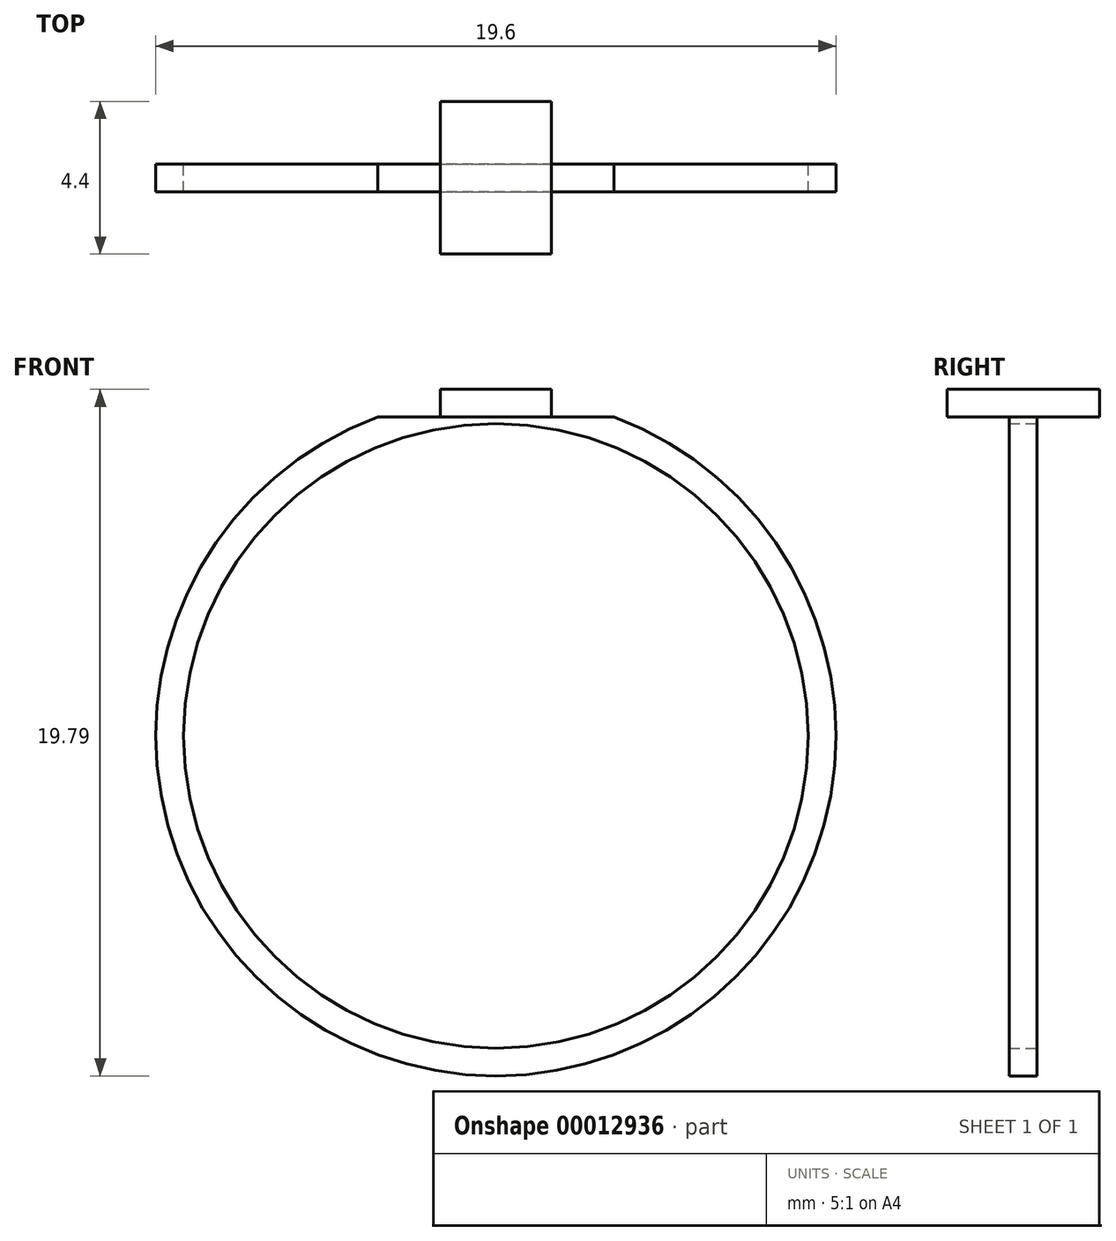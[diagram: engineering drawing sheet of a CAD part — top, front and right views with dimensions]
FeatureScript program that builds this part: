
annotation { "Feature Type Name" : "Feature", "Feature Type Description" : "" }
export const myFeature = defineFeature(function(context is Context, id is Id, definition is map)
    precondition{}
    {
        {
            var Q0;
            Q0=qCreatedBy(makeId("Front.planeOp"),FACE);
            var sketch = newSketch(context, id + "F0", { "sketchPlane" : qUnion([Q0])});
            skCircle(sketch, "E0", {"center": v(0, 0) * mm, "radius": 9 * mm});
            skCircle(sketch, "E1", {"center": v(0, 0) * mm, "radius": 9.8 * mm});
            skLineSegment(sketch, "E2", {"start": v(-3.4, 9.19) * mm, "end": v(3.4, 9.19) * mm});
            skLineSegment(sketch, "E3", {"start": v(0, 0) * mm, "end": v(3.4, 9.19) * mm});
            skLineSegment(sketch, "E4", {"start": v(-3.4, 9.19) * mm, "end": v(0, 0) * mm});
            skSolve(sketch);
        }
        {
            var Q0;
            {var subQ1=sQuery(id+"F0.wireOp",EDGE,"E0");var subQ6=sQuery(id+"F0.wireOp",EDGE,"E3");var subQ7=makeQuery(id+"F0.imprint","INTERSECT",VERTEX,{"derivedFrom":[subQ1,subQ6]});Q0=makeQuery(id+"F0.imprint","IMPRINT",FACE,{"disambiguationData":[TD([[makeQuery(id+"F0.imprint","IMPRINT",EDGE,{"disambiguationData":[TD([[subQ7,1.0]])],"derivedFrom":subQ1}),-1.0]])]});}
            var Q1;
            {var subQ4=sQuery(id+"F0.wireOp",EDGE,"E2");Q1=makeQuery(id+"F0.imprint","IMPRINT",FACE,{"disambiguationData":[TD([[makeQuery(id+"F0.imprint","IMPRINT",EDGE,{"derivedFrom":subQ4}),-1.0]])]});}
            extrude(context, id + "F1", {"entities" : qUnion([Q0, Q1]), "depth" : .4 * mm, "hasSecondDirection" : true, "secondDirectionOppositeDirection" : true, "secondDirectionDepth" : .4 * mm});
        }
        {
            var Q0;
            Q0=makeQuery(id+"F1.opExtrude","SWEPT_FACE",FACE,{"disambiguationData":[OSD([sQuery(id+"F0.wireOp",EDGE,"E2")])]});
            var sketch = newSketch(context, id + "F2", { "sketchPlane" : qUnion([Q0])});
            skLineSegment(sketch, "E5.rect.bottom", {"start": v(1.6, -2.2) * mm, "end": v(-1.6, -2.2) * mm});
            skLineSegment(sketch, "E5.rect.top", {"start": v(1.6, 2.2) * mm, "end": v(-1.6, 2.2) * mm});
            skLineSegment(sketch, "E5.rect.left", {"start": v(1.6, -2.2) * mm, "end": v(1.6, 2.2) * mm});
            skLineSegment(sketch, "E5.rect.right", {"start": v(-1.6, -2.2) * mm, "end": v(-1.6, 2.2) * mm});
            skPoint(sketch, "E5.rect.middle", {"position": v(0, 0) * mm});
            skSolve(sketch);
        }
        {
            var Q0;
            Q0 = qSketchRegion(id + "F2", true);
            extrude(context, id + "F3", {"entities" : qUnion([Q0]), "operationType" : NewBodyOperationType.ADD, "depth" : .8 * mm});
        }
    });
